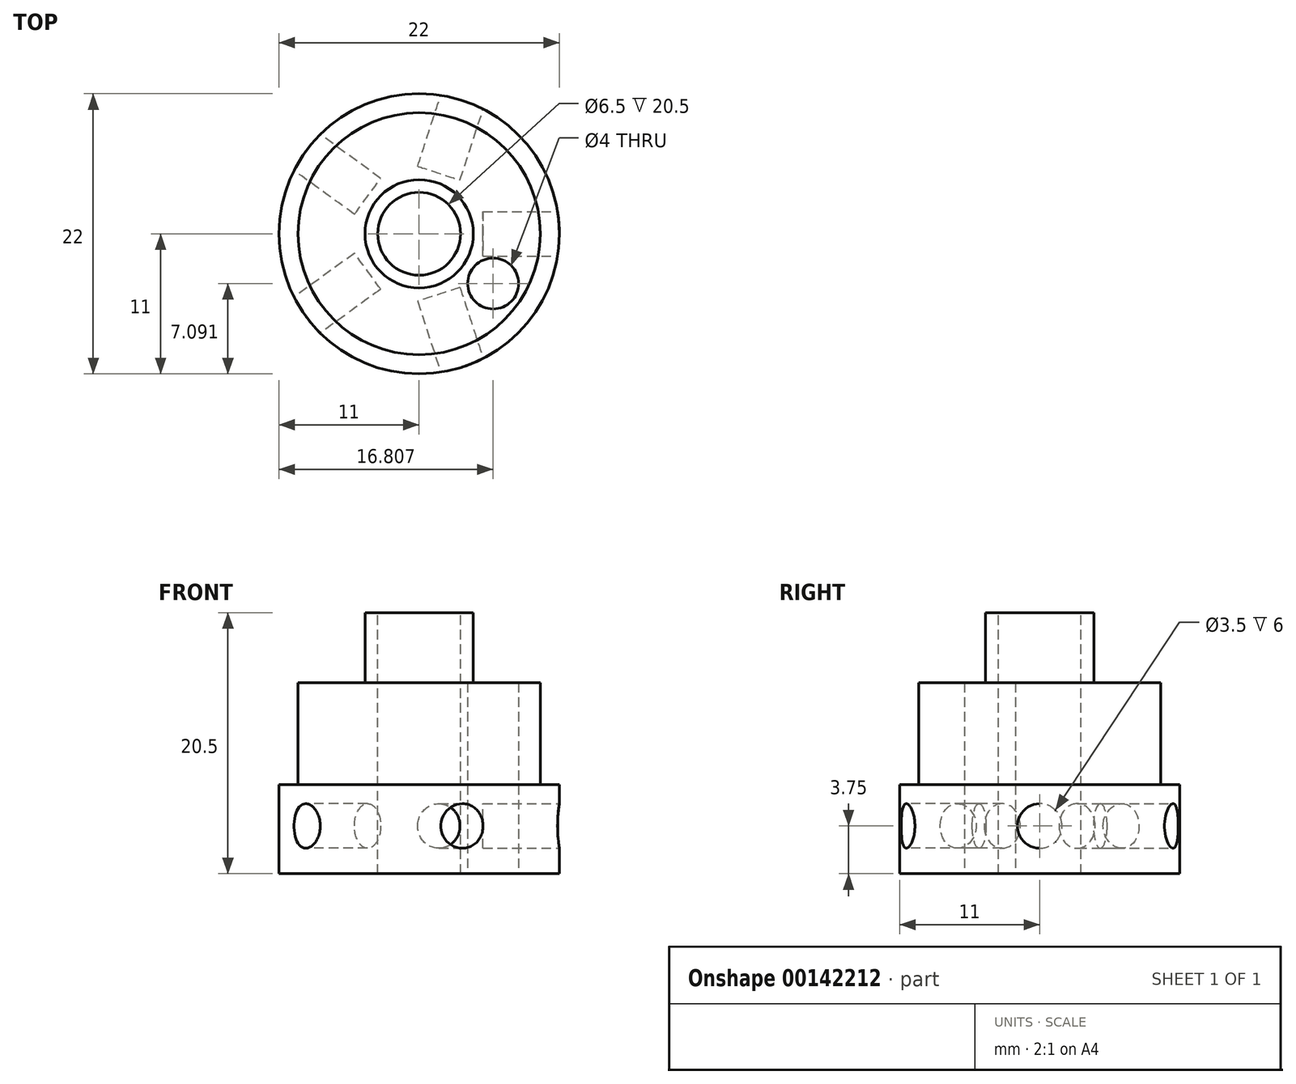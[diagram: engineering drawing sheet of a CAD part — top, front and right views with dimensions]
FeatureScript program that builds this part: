
annotation { "Feature Type Name" : "Feature", "Feature Type Description" : "" }
export const myFeature = defineFeature(function(context is Context, id is Id, definition is map)
    precondition{}
    {
        {
            var Q0;
            Q0=qCreatedBy(makeId("Top.planeOp"),FACE);
            var sketch = newSketch(context, id + "F0", { "sketchPlane" : qUnion([Q0])});
            skCircle(sketch, "E0", {"center": v(0, 0) * mm, "radius": 11 * mm});
            skSolve(sketch);
        }
        {
            var Q0;
            Q0=qSketchRegion(id+"F0",true);
            extrude(context, id + "F1", {"entities" : qUnion([Q0]), "depth" : 7 * mm});
        }
        {
            var Q0;
            Q0=makeQuery(id+"F1.opExtrude","CAP_FACE",FACE,{"disambiguationData":[OSD([sQuery(id+"F0.wireOp",EDGE,"E0")])],"isStart":false});
            var sketch = newSketch(context, id + "F2", { "sketchPlane" : qUnion([Q0])});
            skCircle(sketch, "E1", {"center": v(0, 0) * mm, "radius": 9.5 * mm});
            skSolve(sketch);
        }
        {
            var Q0;
            Q0=qSketchRegion(id+"F2",true);
            extrude(context, id + "F3", {"entities" : qUnion([Q0]), "operationType" : NewBodyOperationType.ADD, "depth" : 8 * mm});
        }
        {
            var Q0;
            Q0=makeQuery(id+"F3.opExtrude","CAP_FACE",FACE,{"disambiguationData":[OSD([sQuery(id+"F2.wireOp",EDGE,"E1")])],"isStart":false});
            var sketch = newSketch(context, id + "F4", { "sketchPlane" : qUnion([Q0])});
            skCircle(sketch, "E2", {"center": v(0, 0) * mm, "radius": 4.25 * mm});
            skSolve(sketch);
        }
        {
            var Q0;
            Q0=qSketchRegion(id+"F4",true);
            extrude(context, id + "F5", {"entities" : qUnion([Q0]), "operationType" : NewBodyOperationType.ADD, "depth" : 5.5 * mm});
        }
        {
            var Q0;
            Q0=makeQuery(id+"F5.opExtrude","CAP_FACE",FACE,{"disambiguationData":[OSD([sQuery(id+"F4.wireOp",EDGE,"E2")])],"isStart":false});
            var sketch = newSketch(context, id + "F6", { "sketchPlane" : qUnion([Q0])});
            skCircle(sketch, "E3", {"center": v(0, 0) * mm, "radius": 3.25 * mm});
            skSolve(sketch);
        }
        {
            var Q0;
            Q0=qSketchRegion(id+"F6",true);
            extrude(context, id + "F7", {"entities" : qUnion([Q0]), "operationType" : NewBodyOperationType.REMOVE, "endBound" : BoundingType.THROUGH_ALL, "oppositeDirection" : true, "depth" : 25 * mm});
        }
        {
            var Q0;
            Q0=makeQuery(id+"F1.opExtrude","CAP_FACE",FACE,{"disambiguationData":[OSD([sQuery(id+"F0.wireOp",EDGE,"E0")])],"isStart":true});
            var sketch = newSketch(context, id + "F8", { "sketchPlane" : qUnion([Q0])});
            skLineSegment(sketch, "E4", {"start": v(0, 0) * mm, "end": v(11, 0) * mm, "construction": true});
            skLineSegment(sketch, "E5", {"start": v(0, 0) * mm, "end": v(3.4, 10.46) * mm, "construction": true});
            skLineSegment(sketch, "E6", {"start": v(0, 0) * mm, "end": v(-8.9, 6.47) * mm, "construction": true});
            skLineSegment(sketch, "E7", {"start": v(0, 0) * mm, "end": v(-8.9, -6.47) * mm, "construction": true});
            skLineSegment(sketch, "E8", {"start": v(0, 0) * mm, "end": v(3.4, -10.46) * mm, "construction": true});
            skLineSegment(sketch, "E9", {"start": v(11, 3.63) * mm, "end": v(11, -3.46) * mm, "construction": true});
            skLineSegment(sketch, "E10", {"start": v(3.4, 10.46) * mm, "end": v(0.34, 11.46) * mm, "construction": true});
            skLineSegment(sketch, "E11", {"start": v(3.4, 10.46) * mm, "end": v(7.1, 9.26) * mm, "construction": true});
            skLineSegment(sketch, "E12", {"start": v(-8.9, 6.47) * mm, "end": v(-6.72, 9.46) * mm, "construction": true});
            skLineSegment(sketch, "E13", {"start": v(-8.9, -6.47) * mm, "end": v(-11, -3.57) * mm, "construction": true});
            skLineSegment(sketch, "E14", {"start": v(3.4, -10.46) * mm, "end": v(7.2, -9.23) * mm, "construction": true});
            skSolve(sketch);
        }
        {
            var Q0;
            Q0=sQuery(id+"F8.wireOp",EDGE,"E9");
            cPlane(context, id + "F9", {"entities" : qUnion([Q0]), "cplaneType" : CPlaneType.LINE_ANGLE, "offset" : 25 * mm, "angle" : 90 * degree, "width" : 150 * mm, "height" : 150 * mm});
        }
        {
            var Q0;
            Q0=qCreatedBy(id+"F9.planeOp",FACE);
            var sketch = newSketch(context, id + "F10", { "sketchPlane" : qUnion([Q0])});
            skCircle(sketch, "E15", {"center": v(0, 3.75) * mm, "radius": 1.75 * mm});
            skSolve(sketch);
        }
        {
            var Q0;
            Q0=sQuery(id+"F8.wireOp",EDGE,"E11");
            cPlane(context, id + "F11", {"entities" : qUnion([Q0]), "cplaneType" : CPlaneType.LINE_ANGLE, "offset" : 25 * mm, "angle" : 0 * degree, "width" : 150 * mm, "height" : 150 * mm});
        }
        {
            var Q0;
            Q0=qCreatedBy(id+"F11.planeOp",FACE);
            var sketch = newSketch(context, id + "F12", { "sketchPlane" : qUnion([Q0])});
            skCircle(sketch, "E16", {"center": v(0, 3.75) * mm, "radius": 1.75 * mm});
            skSolve(sketch);
        }
        {
            var Q0;
            Q0=sQuery(id+"F8.wireOp",EDGE,"E12");
            cPlane(context, id + "F13", {"entities" : qUnion([Q0]), "cplaneType" : CPlaneType.LINE_ANGLE, "offset" : 25 * mm, "angle" : 90 * degree, "width" : 150 * mm, "height" : 150 * mm});
        }
        {
            var Q0;
            Q0=qCreatedBy(id+"F13.planeOp",FACE);
            var sketch = newSketch(context, id + "F14", { "sketchPlane" : qUnion([Q0])});
            skCircle(sketch, "E17", {"center": v(0, 3.75) * mm, "radius": 1.75 * mm});
            skSolve(sketch);
        }
        {
            var Q0;
            Q0=sQuery(id+"F8.wireOp",EDGE,"E13");
            cPlane(context, id + "F15", {"entities" : qUnion([Q0]), "cplaneType" : CPlaneType.LINE_ANGLE, "offset" : 25 * mm, "angle" : 90 * degree, "width" : 150 * mm, "height" : 150 * mm});
        }
        {
            var Q0;
            Q0=qCreatedBy(id+"F15.planeOp",FACE);
            var sketch = newSketch(context, id + "F16", { "sketchPlane" : qUnion([Q0])});
            skCircle(sketch, "E18", {"center": v(0, 3.75) * mm, "radius": 1.75 * mm});
            skSolve(sketch);
        }
        {
            var Q0;
            Q0=sQuery(id+"F8.wireOp",EDGE,"E14");
            cPlane(context, id + "F17", {"entities" : qUnion([Q0]), "cplaneType" : CPlaneType.LINE_ANGLE, "offset" : 25 * mm, "angle" : 0 * degree, "width" : 150 * mm, "height" : 150 * mm});
        }
        {
            var Q0;
            Q0=qCreatedBy(id+"F17.planeOp",FACE);
            var sketch = newSketch(context, id + "F18", { "sketchPlane" : qUnion([Q0])});
            skCircle(sketch, "E19", {"center": v(0, 3.75) * mm, "radius": 1.75 * mm});
            skSolve(sketch);
        }
        {
            var Q0;
            Q0=makeQuery(id+"F10.imprint","IMPRINT",FACE,{"disambiguationData":[TD([[makeQuery(id+"F10.imprint","IMPRINT",EDGE,{"derivedFrom":sQuery(id+"F10.wireOp",EDGE,"E15")}),1.0]])]});
            extrude(context, id + "F19", {"entities" : qUnion([Q0]), "operationType" : NewBodyOperationType.REMOVE, "oppositeDirection" : true, "depth" : 6 * mm});
        }
        {
            var Q0;
            Q0=makeQuery(id+"F12.imprint","IMPRINT",FACE,{"disambiguationData":[TD([[makeQuery(id+"F12.imprint","IMPRINT",EDGE,{"derivedFrom":sQuery(id+"F12.wireOp",EDGE,"E16")}),1.0]])]});
            extrude(context, id + "F20", {"entities" : qUnion([Q0]), "operationType" : NewBodyOperationType.REMOVE, "depth" : 6 * mm});
        }
        {
            var Q0;
            Q0=makeQuery(id+"F14.imprint","IMPRINT",FACE,{"disambiguationData":[TD([[makeQuery(id+"F14.imprint","IMPRINT",EDGE,{"derivedFrom":sQuery(id+"F14.wireOp",EDGE,"E17")}),1.0]])]});
            extrude(context, id + "F21", {"entities" : qUnion([Q0]), "operationType" : NewBodyOperationType.REMOVE, "depth" : 6 * mm});
        }
        {
            var Q0;
            Q0=makeQuery(id+"F16.imprint","IMPRINT",FACE,{"disambiguationData":[TD([[makeQuery(id+"F16.imprint","IMPRINT",EDGE,{"derivedFrom":sQuery(id+"F16.wireOp",EDGE,"E18")}),1.0]])]});
            extrude(context, id + "F22", {"entities" : qUnion([Q0]), "operationType" : NewBodyOperationType.REMOVE, "depth" : 6 * mm});
        }
        {
            var Q0;
            Q0=makeQuery(id+"F18.imprint","IMPRINT",FACE,{"disambiguationData":[TD([[makeQuery(id+"F18.imprint","IMPRINT",EDGE,{"derivedFrom":sQuery(id+"F18.wireOp",EDGE,"E19")}),1.0]])]});
            extrude(context, id + "F23", {"entities" : qUnion([Q0]), "operationType" : NewBodyOperationType.REMOVE, "oppositeDirection" : true, "depth" : 6 * mm});
        }
        {
            var Q0;
            {var subQ0=sQuery(id+"F0.wireOp",EDGE,"E0");Q0=makeQuery(id+"F8.imprint","IMPRINT",FACE,{"disambiguationData":[TD([[makeQuery(id+"F8.imprint","IMPRINT",EDGE,{"derivedFrom":makeQuery(id+"F1.opExtrude","CAP_EDGE",EDGE,{"disambiguationData":[OSD([subQ0])],"isStart":true})}),-1.0]])]});}
            var sketch = newSketch(context, id + "F24", { "sketchPlane" : qUnion([Q0])});
            skPoint(sketch, "E20.0", {"position": v(11, 0) * mm});
            skLineSegment(sketch, "E21", {"start": v(11, 0) * mm, "end": v(5.8, 3.9) * mm, "construction": true});
            skCircle(sketch, "E22", {"center": v(5.8, 3.9) * mm, "radius": 2 * mm});
            skLineSegment(sketch, "E23", {"start": v(0, 0) * mm, "end": v(5.8, 3.9) * mm, "construction": true});
            skSolve(sketch);
        }
        {
            var Q0;
            Q0=qSketchRegion(id+"F24",true);
            extrude(context, id + "F25", {"entities" : qUnion([Q0]), "operationType" : NewBodyOperationType.REMOVE, "oppositeDirection" : true, "depth" : 25 * mm});
        }
    });
